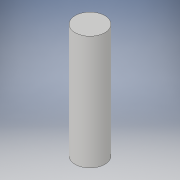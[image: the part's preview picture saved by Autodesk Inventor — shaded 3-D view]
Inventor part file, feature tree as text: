
AUTODESK INVENTOR PART (.ipt)
format: ipt  version: 2019 (Build 230136000, 136)  size: 88,576 bytes
history: native  units: in
note: dims shown in document units (in); Inventor stores cm internally (conversion verified against a paired STEP export)
features: extrude x1, sketch x1
ambient origin geometry x8: Origin, YZ Plane, XZ Plane, XY Plane, X Axis, Y Axis, Z Axis, Center Point
bodies: Solid1 (feature_tree)
feature tree (2):
  extrude  "Extrusion1"  Depth=7.874in TaperAngle=0.0deg
  sketch  "Sketch1"  dims[d0=2.0472in d1=7.874in d2=0.0in]
